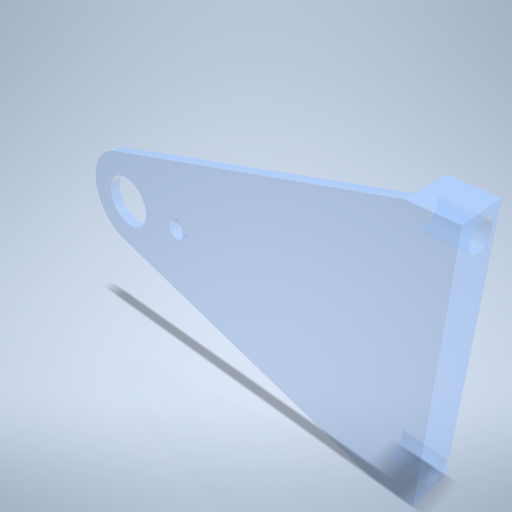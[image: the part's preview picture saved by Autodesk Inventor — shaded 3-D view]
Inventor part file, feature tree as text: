
AUTODESK INVENTOR PART (.ipt)
format: ipt  version: 2024.2 (Build 282272000, 272)  size: 284,160 bytes
history: native  units: mm
features: sketch x5, hole x3, extrude x2
ambient origin geometry x8: Origin, YZ Plane, XZ Plane, XY Plane, X Axis, Y Axis, Z Axis, Center Point
bodies: Volumenkörper1 (feature_tree)
feature tree (10):
  extrude  "Extrusion1"  Depth=50.0mm
  extrude  "Extrusion2"  Depth=65.0mm
  hole  "Bohrung1"  [1 undecoded]
  hole  "Bohrung2"  [1 undecoded]
  hole  "Bohrung3"  [1 undecoded]
  sketch  "Skizze1"  dims[d0=9.5mm d1=50.0mm]
  sketch  "Skizze2"  dims[d2=8.0mm d3=65.0mm]
  sketch  "Skizze3"  dims[d4=2.0mm d5=0.0mm d6=6.5mm d7=0.0mm]
  sketch  "Skizze4"  dims[d8=5.0mm d9=6.0mm d10=4.0mm d11=2.0mm d12=90.0deg d13=8.0mm d14=0.0mm d15=5.0mm]
  sketch  "Skizze5"  dims[d18=10.0mm d19=6.0mm d20=4.0mm d21=2.0mm d22=90.0deg d23=8.0mm d24=0.0mm d25=3.5mm d26=6.0mm d27=4.0mm d28=2.0mm d29=90.0deg d30=8.0mm d31=0.0mm d32=13.029967mm d33=42.248mm]
note: 3 required parameter values undecoded (feature->parameter linkage not recoverable at this tier; creation-order binding heuristic only, values carry confidence <= 0.55)
